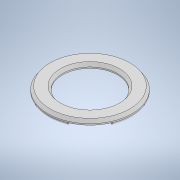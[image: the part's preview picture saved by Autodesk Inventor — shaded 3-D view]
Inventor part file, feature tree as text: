
AUTODESK INVENTOR PART (.ipt)
format: ipt  version: 2020 (Build 240168000, 168)  size: 199,680 bytes
history: native  units: mm
features: projected_geometry x4, revolve x3, sketch x3, chamfer x2, other x1, pattern_circular x1
ambient origin geometry x8: Origin, YZ Plane, XZ Plane, XY Plane, X Axis, Y Axis, Z Axis, Center Point
bodies: Body1 (feature_tree)
feature tree (14):
  other  "Твердое тело1"
  revolve  "Вращение1"
  chamfer  "Фаска1"  Distance=10.0mm
  revolve  "Вращение2"
  pattern_circular  "Круговой массив1"  [2 undecoded]
  revolve  "Вращение3"
  chamfer  "Фаска2"  Distance=2.0mm
  sketch  "Эскиз1"
  sketch  "Эскиз2"
  projected_geometry  "Спроецированная петля1"
  projected_geometry  "Спроецированная петля2"
  projected_geometry  "Спроецированная петля3"
  sketch  "Эскиз3"
  projected_geometry  "Спроецированная петля4"
note: 2 required parameter values undecoded (feature->parameter linkage not recoverable at this tier; creation-order binding heuristic only, values carry confidence <= 0.55)
